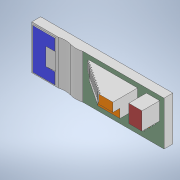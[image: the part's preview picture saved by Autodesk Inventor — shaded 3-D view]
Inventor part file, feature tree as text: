
AUTODESK INVENTOR PART (.ipt)
format: ipt  version: 2021 (Build 250183000, 183)  size: 261,632 bytes
history: native  units: mm
features: extrude x11, sketch x10, other x1
ambient origin geometry x8: Origin, YZ Plane, XZ Plane, XY Plane, X Axis, Y Axis, Z Axis, Center Point
bodies: Body1 (feature_tree)
feature tree (22):
  other  "ソリッド1"
  extrude  "押し出し1"  Depth=5000.0mm
  extrude  "押し出し2"  Depth=1000.0mm
  extrude  "押し出し3"  Depth=15000.0mm
  extrude  "押し出し4"  Depth=1000.0mm TaperAngle=0.0deg
  extrude  "押し出し5"  Depth=2000.0mm TaperAngle=0.0deg
  extrude  "押し出し6"  Depth=2000.0mm TaperAngle=0.0deg
  extrude  "押し出し7"  Depth=1000.0mm TaperAngle=0.0deg
  extrude  "押し出し8"  Depth=80.0mm
  extrude  "押し出し9"  Depth=80.0mm
  extrude  "押し出し10"  Depth=80.0mm
  extrude  "押し出し11"  Depth=80.0mm
  sketch  "スケッチ1"
  sketch  "スケッチ2"
  sketch  "スケッチ3"
  sketch  "スケッチ4"
  sketch  "スケッチ5"
  sketch  "スケッチ6"
  sketch  "スケッチ7"
  sketch  "スケッチ8"
  sketch  "スケッチ9"
  sketch  "スケッチ12"
